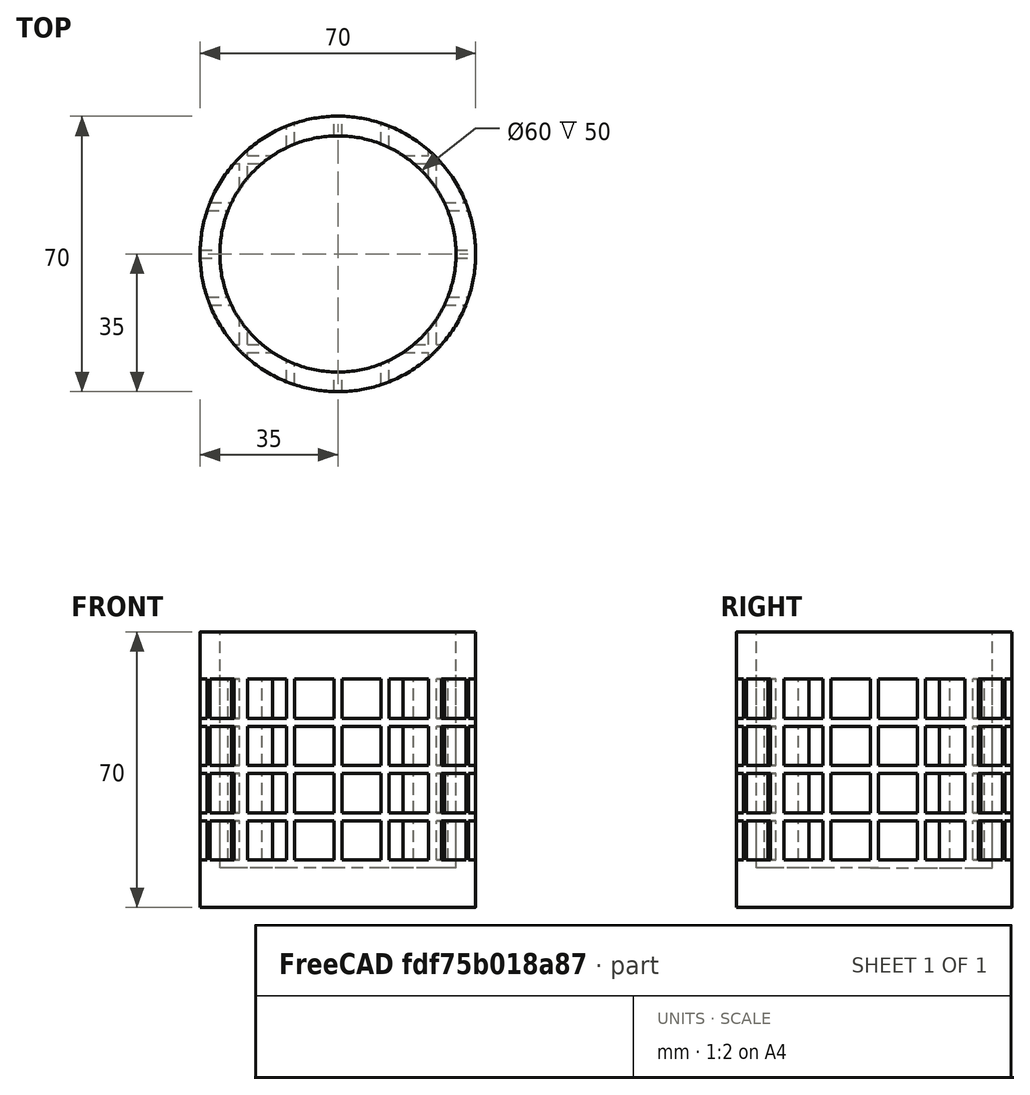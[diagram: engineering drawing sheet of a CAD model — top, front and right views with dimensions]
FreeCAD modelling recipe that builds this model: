
FCSTD DOCUMENT  (FreeCAD 0.14R3702 (Git))
Label: vaso
License: CC-BY 3.0
LicenseURL: http://creativecommons.org/licenses/by/3.0/
objects: Part::Cylinder×5, Part::Cut×3, Part::Box×2, Part::FeaturePython×1, Part::MultiCommon×1, Part::MultiFuse×1
note: 13 computed .brp shape members not serialized (recipe doc carries the construction recipe); baked Part::Feature solids carry a one-line shape summary decoded from their .brp

FEATURE [Part::Box] Box  label="Cubo"
  Height = 10
  Length = 10
  Width = 10
FEATURE [Part::FeaturePython] Array  # Draft array (typed FeaturePython)
  Angle = 360
  ArrayType = 0
  Axis = (0,0,1)
  Base = -> Box
  Center = (0,0,0)
  IntervalX = (12,0,0)
  IntervalY = (0,12,0)
  IntervalZ = (0,0,12)
  NumberPolar = 0
  NumberX = 6
  NumberY = 6
  NumberZ = 6
  Placement = pos=(-35,-35,0) rot=(0,0,1;0rad)
FEATURE [Part::Box] Box001  label="Cubo001"
  Height = 70
  Length = 70
  Placement = pos=(-35,-35,0) rot=(0,0,1;0rad)
  Width = 70
FEATURE [Part::Cut] Cut
  Base = -> Box001
  Tool = -> Array
FEATURE [Part::Cylinder] Cylinder  label="Cilindro"
  Angle = 360
  Height = 70
  Radius = 30
FEATURE [Part::Cut] Cut001
  Base = -> Cut
  Tool = -> Cylinder
FEATURE [Part::Cylinder] Cylinder001  label="Cilindro001"
  Angle = 360
  Height = 70
  Radius = 35
FEATURE [Part::MultiCommon] Common
  Shapes = -> [Cut001,Cylinder001]
FEATURE [Part::Cylinder] Cylinder002  label="Cilindro002"
  Angle = 360
  Height = 10
  Radius = 35
FEATURE [Part::Cylinder] Cylinder003  label="Cilindro003"
  Angle = 360
  Height = 10
  Placement = pos=(0,0,60) rot=(0,0,1;0rad)
  Radius = 35
FEATURE [Part::Cylinder] Cylinder004  label="Cilindro004"
  Angle = 360
  Height = 10
  Placement = pos=(0,0,60) rot=(0,0,1;0rad)
  Radius = 30
FEATURE [Part::Cut] Cut002
  Base = -> Cylinder003
  Tool = -> Cylinder004
FEATURE [Part::MultiFuse] Fusion
  Shapes = -> [Cut002,Cylinder002,Common]
